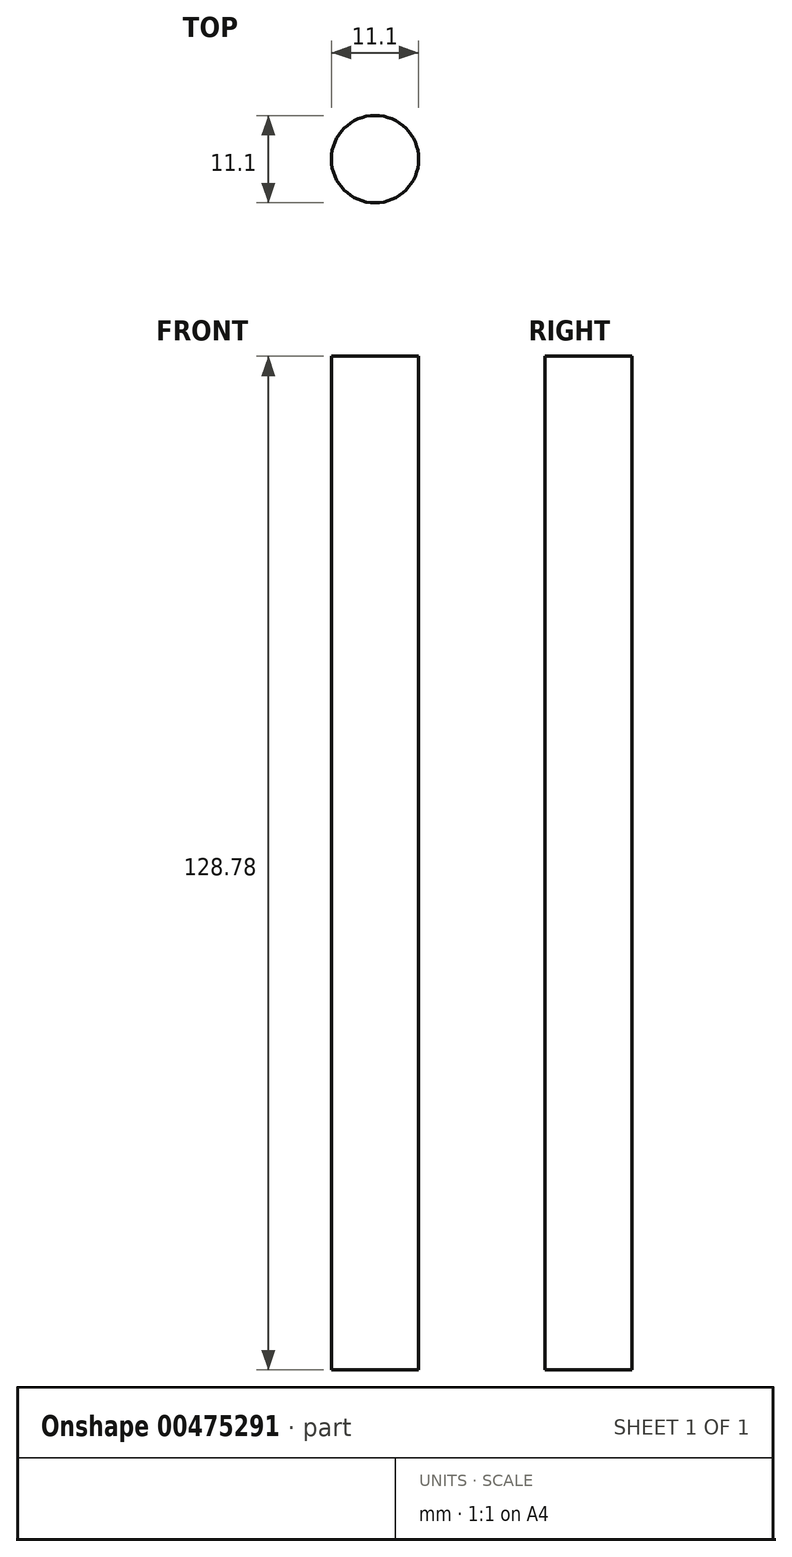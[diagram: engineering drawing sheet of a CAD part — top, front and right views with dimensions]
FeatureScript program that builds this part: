
annotation { "Feature Type Name" : "Feature", "Feature Type Description" : "" }
export const myFeature = defineFeature(function(context is Context, id is Id, definition is map)
    precondition{}
    {
        {
            var Q0;
            Q0=qCreatedBy(makeId("Top.planeOp"),FACE);
            var sketch = newSketch(context, id + "F0", { "sketchPlane" : qUnion([Q0])});
            skCircle(sketch, "E0", {"center": v(0, 0) * mm, "radius": 5.55 * mm});
            skSolve(sketch);
        }
        {
            var Q0;
            Q0 = qSketchRegion(id + "F0", true);
            extrude(context, id + "F1", {"entities" : qUnion([Q0]), "depth" : 128.78 * mm});
        }
    });
